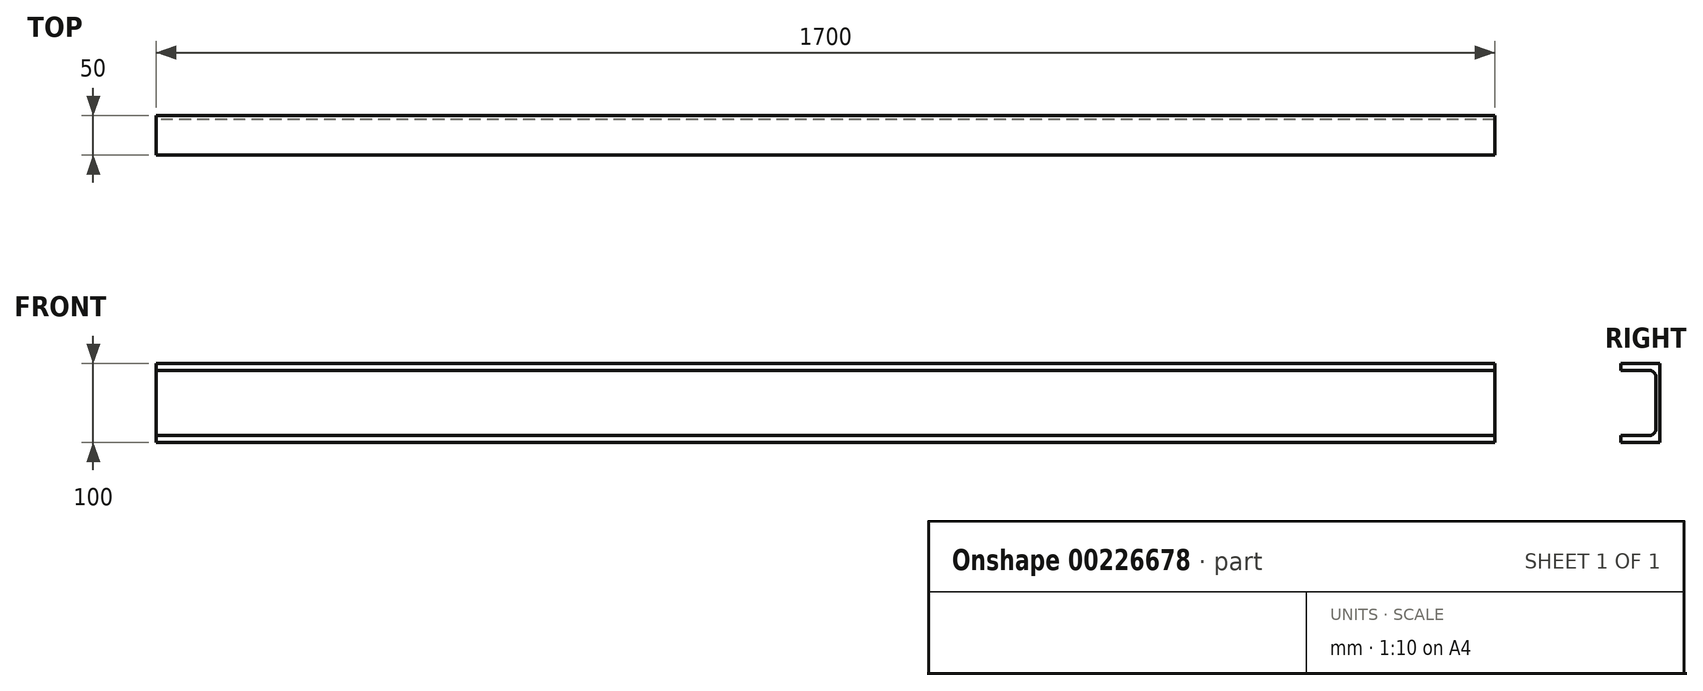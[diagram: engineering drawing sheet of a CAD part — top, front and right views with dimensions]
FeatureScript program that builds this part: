
annotation { "Feature Type Name" : "Feature", "Feature Type Description" : "" }
export const myFeature = defineFeature(function(context is Context, id is Id, definition is map)
    precondition{}
    {
        {
            var Q0;
            Q0=qCreatedBy(makeId("Right.planeOp"),FACE);
            var sketch = newSketch(context, id + "F0", { "sketchPlane" : qUnion([Q0])});
            skLineSegment(sketch, "E0", {"start": v(-20.57, 55.3) * mm, "end": v(29.43, 55.3) * mm});
            skLineSegment(sketch, "E1", {"start": v(29.43, 55.3) * mm, "end": v(29.43, -44.7) * mm});
            skLineSegment(sketch, "E2", {"start": v(29.43, -44.7) * mm, "end": v(-20.57, -44.7) * mm});
            skLineSegment(sketch, "E3", {"start": v(-20.57, -44.7) * mm, "end": v(-20.57, -36.2) * mm});
            skLineSegment(sketch, "E4", {"start": v(-20.57, -36.2) * mm, "end": v(15.43, -36.2) * mm});
            skLineSegment(sketch, "E5", {"start": v(-20.57, 55.3) * mm, "end": v(-20.57, 46.8) * mm});
            skLineSegment(sketch, "E6", {"start": v(-20.57, 46.8) * mm, "end": v(15.43, 46.8) * mm});
            skLineSegment(sketch, "E7", {"start": v(24.43, 37.8) * mm, "end": v(24.43, -27.2) * mm});
            skPoint(sketch, "E8.visualSharp", {"position": v(24.43, 46.8) * mm});
            skArc(sketch, "E8.filletArc", {"start": v(24.43, 37.8) * mm, "mid": v(21.8, 44.16) * mm, "end": v(15.43, 46.8) * mm});
            skPoint(sketch, "E9.visualSharp", {"position": v(24.43, -36.2) * mm});
            skArc(sketch, "E9.filletArc", {"start": v(15.43, -36.2) * mm, "mid": v(21.8, -33.57) * mm, "end": v(24.43, -27.2) * mm});
            skSolve(sketch);
        }
        {
            var Q0;
            Q0=makeQuery(id+"F0.imprint","IMPRINT",FACE,{"disambiguationData":[TD([[makeQuery(id+"F0.imprint","IMPRINT",EDGE,{"derivedFrom":sQuery(id+"F0.wireOp",EDGE,"E0")}),-1.0]])]});
            extrude(context, id + "F1", {"entities" : qUnion([Q0]), "depth" : 1700 * mm});
        }
    });
